# Revit family: Скамейка стальная «Энигма» Арт 14121
name_source: partatom
category: Антураж
revit_build: Autodesk Revit 2018 (Build: 20180423_1000(x64)
units: mm (PartAtom-declared; Revit-internal decimal feet)

## family parameters
Всегда вертикально = Да
Источник визуального образа = Геометрия семейства
На основе рабочей плоскости = Нет
Общий = Нет
При загрузке вырезать с полостями = Нет
Точка расчета площади = Нет

## types (4) — shared parameters
URL = https://hobbyka.ru
Артикул товара = Арт. 14121
Высота = 840 мм
Группа модели = Скамейки
Изготовитель = ООО «Хоббика»
Изображение типоразмера = 68ce0d10d25cda0047d66e55ffdcb8d4.jpg
Материал изделия = Дерево, сталь
Цвет каркаса = Сталь
Цвет лавки = Орех
Ширина = 610 мм

## per-type parameters (varying)
| type | Версия 1,5 м | Версия 1,8 м | Версия 2,0 м | Версия 3,0 м | Длина | Описание |
| Скамейка стальная «Энигма» 1,5 м | Да | Нет | Нет | Нет | 1500 мм | Скамейка стальная «Энигма». Модель 1,5 м |
| Скамейка стальная «Энигма» 1,8 м | Нет | Да | Нет | Нет | 1800 мм | Скамейка стальная «Энигма». Модель 1,8 м |
| Скамейка стальная «Энигма» 2,0 м | Нет | Нет | Да | Нет | 2000 мм | Скамейка стальная «Энигма». Модель 2,0 м |
| Скамейка стальная «Энигма» 3,0 м | Нет | Нет | Нет | Да | 3000 мм | Скамейка стальная «Энигма». Модель 3,0 м |
